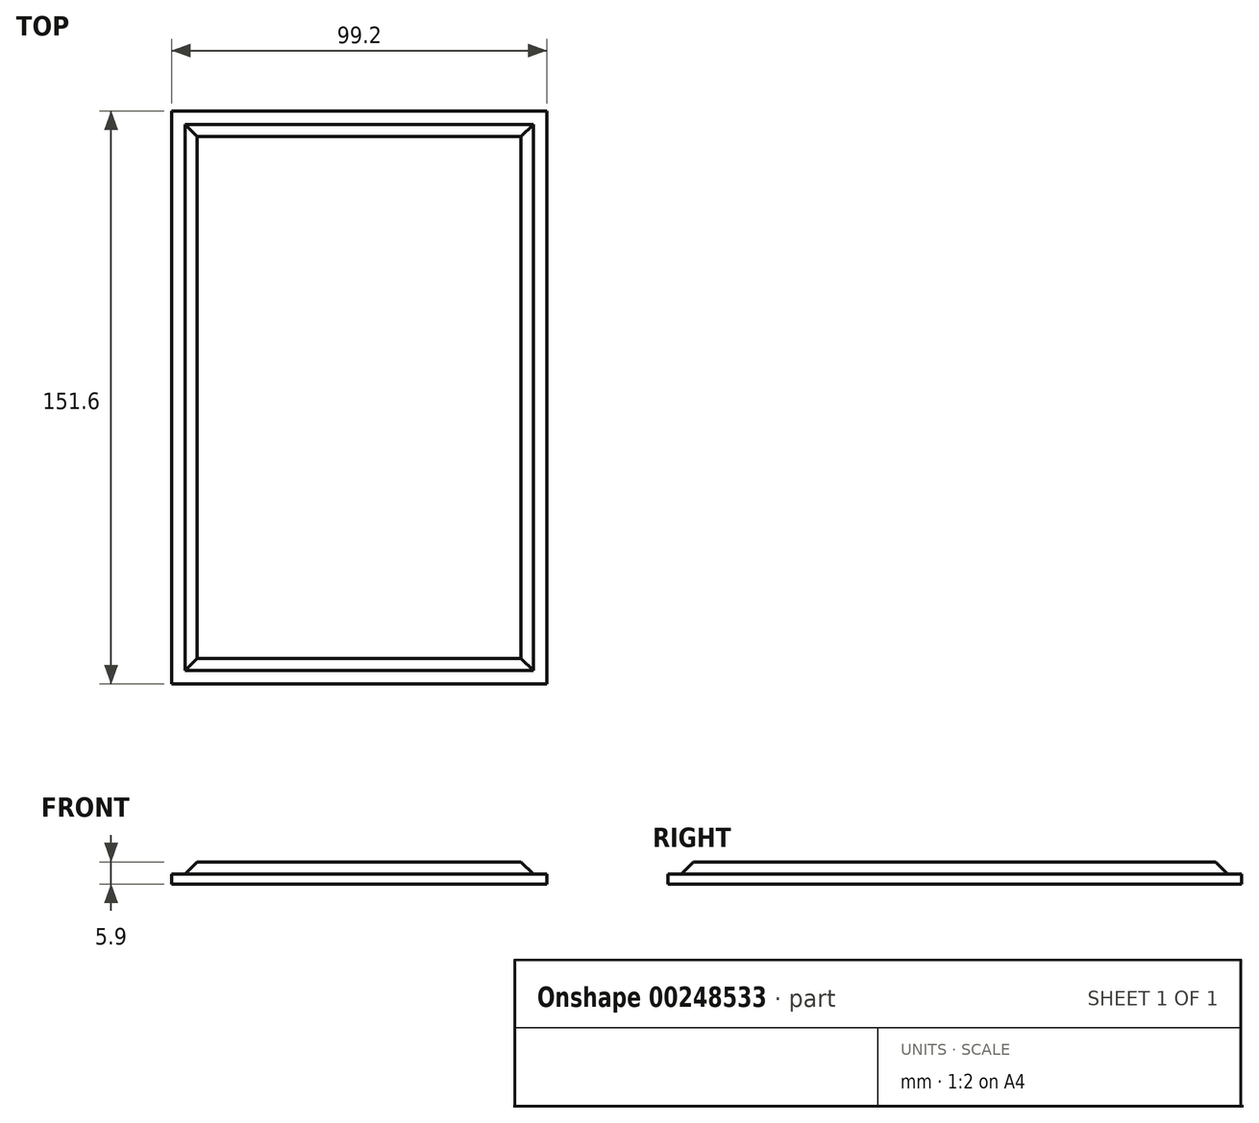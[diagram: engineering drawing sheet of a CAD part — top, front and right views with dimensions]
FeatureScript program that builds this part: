
annotation { "Feature Type Name" : "Feature", "Feature Type Description" : "" }
export const myFeature = defineFeature(function(context is Context, id is Id, definition is map)
    precondition{}
    {
        {
            var Q0;
            Q0=qCreatedBy(makeId("Top.planeOp"),FACE);
            var sketch = newSketch(context, id + "F0", { "sketchPlane" : qUnion([Q0])});
            skLineSegment(sketch, "E0.bottom", {"start": v(46, 72.2) * mm, "end": v(-46, 72.2) * mm});
            skLineSegment(sketch, "E0.top", {"start": v(46, -72.2) * mm, "end": v(-46, -72.2) * mm});
            skLineSegment(sketch, "E0.left", {"start": v(46, 72.2) * mm, "end": v(46, -72.2) * mm});
            skLineSegment(sketch, "E0.right", {"start": v(-46, 72.2) * mm, "end": v(-46, -72.2) * mm});
            skPoint(sketch, "E0.middle", {"position": v(0, 0) * mm});
            skLineSegment(sketch, "E1.bottom", {"start": v(49.6, -75.8) * mm, "end": v(-49.6, -75.8) * mm});
            skLineSegment(sketch, "E1.top", {"start": v(49.6, 75.8) * mm, "end": v(-49.6, 75.8) * mm});
            skLineSegment(sketch, "E1.left", {"start": v(49.6, -75.8) * mm, "end": v(49.6, 75.8) * mm});
            skLineSegment(sketch, "E1.right", {"start": v(-49.6, -75.8) * mm, "end": v(-49.6, 75.8) * mm});
            skLineSegment(sketch, "E2.bottom", {"start": v(-42.8, 69) * mm, "end": v(42.8, 69) * mm});
            skLineSegment(sketch, "E2.top", {"start": v(-42.8, -69) * mm, "end": v(42.8, -69) * mm});
            skLineSegment(sketch, "E2.left", {"start": v(-42.8, 69) * mm, "end": v(-42.8, -69) * mm});
            skLineSegment(sketch, "E2.right", {"start": v(42.8, 69) * mm, "end": v(42.8, -69) * mm});
            skSolve(sketch);
        }
        {
            var Q0;
            Q0=makeQuery(id+"F0.imprint","IMPRINT",FACE,{"disambiguationData":[TD([[makeQuery(id+"F0.imprint","IMPRINT",EDGE,{"derivedFrom":sQuery(id+"F0.wireOp",EDGE,"E0.bottom")}),-1.0]])]});
            var Q1;
            Q1=makeQuery(id+"F0.imprint","IMPRINT",FACE,{"disambiguationData":[TD([[makeQuery(id+"F0.imprint","IMPRINT",EDGE,{"derivedFrom":sQuery(id+"F0.wireOp",EDGE,"E0.bottom")}),1.0]])]});
            var Q2;
            Q2=makeQuery(id+"F0.imprint","IMPRINT",FACE,{"disambiguationData":[TD([[makeQuery(id+"F0.imprint","IMPRINT",EDGE,{"derivedFrom":sQuery(id+"F0.wireOp",EDGE,"E2.bottom")}),-1.0]])]});
            extrude(context, id + "F1", {"entities" : qUnion([Q0, Q1, Q2]), "oppositeDirection" : true, "depth" : 2.7 * mm});
        }
        {
            var Q0;
            Q0=makeQuery(id+"F0.imprint","IMPRINT",FACE,{"disambiguationData":[TD([[makeQuery(id+"F0.imprint","IMPRINT",EDGE,{"derivedFrom":sQuery(id+"F0.wireOp",EDGE,"E0.bottom")}),1.0]])]});
            var Q1;
            Q1=makeQuery(id+"F0.imprint","IMPRINT",FACE,{"disambiguationData":[TD([[makeQuery(id+"F0.imprint","IMPRINT",EDGE,{"derivedFrom":sQuery(id+"F0.wireOp",EDGE,"E2.bottom")}),-1.0]])]});
            extrude(context, id + "F2", {"entities" : qUnion([Q0, Q1]), "operationType" : NewBodyOperationType.ADD, "depth" : 3.2 * mm});
        }
        {
            var Q0;
            Q0=makeQuery(id+"F2.opExtrude","CAP_EDGE",EDGE,{"disambiguationData":[OSD([sQuery(id+"F0.wireOp",EDGE,"E0.top")])],"isStart":false});
            var Q1;
            Q1=makeQuery(id+"F2.opExtrude","CAP_EDGE",EDGE,{"disambiguationData":[OSD([sQuery(id+"F0.wireOp",EDGE,"E0.right")])],"isStart":false});
            var Q2;
            Q2=makeQuery(id+"F2.opExtrude","CAP_EDGE",EDGE,{"disambiguationData":[OSD([sQuery(id+"F0.wireOp",EDGE,"E0.left")])],"isStart":false});
            var Q3;
            Q3=makeQuery(id+"F2.opExtrude","CAP_EDGE",EDGE,{"disambiguationData":[OSD([sQuery(id+"F0.wireOp",EDGE,"E0.bottom")])],"isStart":false});
            chamfer(context, id + "F3", {"entities" : qUnion([Q0, Q1, Q2, Q3]), "width" : 3.2 * mm, "tangentPropagation" : true});
        }
    });
